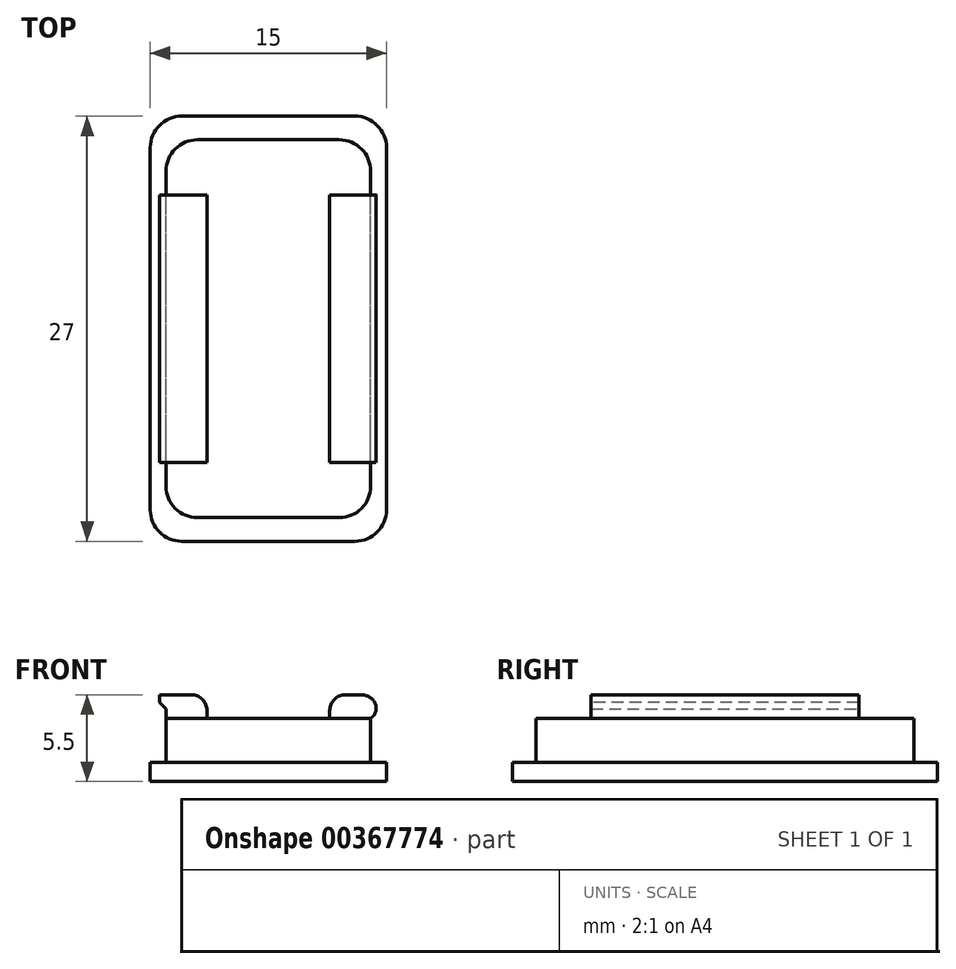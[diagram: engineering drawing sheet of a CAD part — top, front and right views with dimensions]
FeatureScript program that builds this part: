
annotation { "Feature Type Name" : "Feature", "Feature Type Description" : "" }
export const myFeature = defineFeature(function(context is Context, id is Id, definition is map)
    precondition{}
    {
        {
            var Q0;
            Q0=qCreatedBy(makeId("Top.planeOp"),FACE);
            var sketch = newSketch(context, id + "F0", { "sketchPlane" : qUnion([Q0])});
            skLineSegment(sketch, "E0.bottom", {"start": v(6.5, -12) * mm, "end": v(-6.5, -12) * mm});
            skLineSegment(sketch, "E0.top", {"start": v(6.5, 12) * mm, "end": v(-6.5, 12) * mm});
            skLineSegment(sketch, "E0.left", {"start": v(6.5, -12) * mm, "end": v(6.5, 12) * mm});
            skLineSegment(sketch, "E0.right", {"start": v(-6.5, -12) * mm, "end": v(-6.5, 12) * mm});
            skPoint(sketch, "E0.middle", {"position": v(0, 0) * mm});
            skLineSegment(sketch, "E1.bottom", {"start": v(7.5, -13.5) * mm, "end": v(-7.5, -13.5) * mm});
            skLineSegment(sketch, "E1.top", {"start": v(7.5, 13.5) * mm, "end": v(-7.5, 13.5) * mm});
            skLineSegment(sketch, "E1.left", {"start": v(7.5, -13.5) * mm, "end": v(7.5, 13.5) * mm});
            skLineSegment(sketch, "E1.right", {"start": v(-7.5, -13.5) * mm, "end": v(-7.5, 13.5) * mm});
            skSolve(sketch);
        }
        {
            var Q0;
            Q0 = qSketchRegion(id + "F0", true);
            extrude(context, id + "F1", {"entities" : qUnion([Q0]), "depth" : 1.2 * mm});
        }
        {
            var Q0;
            Q0=makeQuery(id+"F0.imprint","IMPRINT",FACE,{"disambiguationData":[TD([[makeQuery(id+"F0.imprint","IMPRINT",EDGE,{"derivedFrom":sQuery(id+"F0.wireOp",EDGE,"E0.bottom")}),-1.0]])]});
            extrude(context, id + "F2", {"entities" : qUnion([Q0]), "operationType" : NewBodyOperationType.ADD, "depth" : 4 * mm});
        }
        {
            var Q0;
            Q0=makeQuery(id+"F2.opExtrude","SWEPT_EDGE",EDGE,{"disambiguationData":[OSD([sQuery(id+"F0.wireOp",EDGE,"E0.top"),sQuery(id+"F0.wireOp",EDGE,"E0.left")])]});
            var Q1;
            Q1=makeQuery(id+"F1.opExtrude","SWEPT_EDGE",EDGE,{"disambiguationData":[OSD([sQuery(id+"F0.wireOp",EDGE,"E1.top"),sQuery(id+"F0.wireOp",EDGE,"E1.left")])]});
            var Q2;
            Q2=makeQuery(id+"F2.opExtrude","SWEPT_EDGE",EDGE,{"disambiguationData":[OSD([sQuery(id+"F0.wireOp",EDGE,"E0.top"),sQuery(id+"F0.wireOp",EDGE,"E0.right")])]});
            var Q3;
            Q3=makeQuery(id+"F1.opExtrude","SWEPT_EDGE",EDGE,{"disambiguationData":[OSD([sQuery(id+"F0.wireOp",EDGE,"E1.top"),sQuery(id+"F0.wireOp",EDGE,"E1.right")])]});
            var Q4;
            Q4=makeQuery(id+"F2.opExtrude","SWEPT_EDGE",EDGE,{"disambiguationData":[OSD([sQuery(id+"F0.wireOp",EDGE,"E0.bottom"),sQuery(id+"F0.wireOp",EDGE,"E0.right")])]});
            var Q5;
            Q5=makeQuery(id+"F1.opExtrude","SWEPT_EDGE",EDGE,{"disambiguationData":[OSD([sQuery(id+"F0.wireOp",EDGE,"E1.bottom"),sQuery(id+"F0.wireOp",EDGE,"E1.right")])]});
            var Q6;
            Q6=makeQuery(id+"F1.opExtrude","SWEPT_EDGE",EDGE,{"disambiguationData":[OSD([sQuery(id+"F0.wireOp",EDGE,"E1.bottom"),sQuery(id+"F0.wireOp",EDGE,"E1.left")])]});
            var Q7;
            Q7=makeQuery(id+"F2.opExtrude","SWEPT_EDGE",EDGE,{"disambiguationData":[OSD([sQuery(id+"F0.wireOp",EDGE,"E0.bottom"),sQuery(id+"F0.wireOp",EDGE,"E0.left")])]});
            fillet(context, id + "F3", {"entities" : qUnion([Q0, Q1, Q2, Q3, Q4, Q5, Q6, Q7]), "radius" : 2 * mm, "tangentPropagation" : true, "allowEdgeOverflow" : false});
        }
        {
            var Q0;
            Q0=makeQuery(id+"F2.opExtrude","CAP_FACE",FACE,{"disambiguationData":[OSD([sQuery(id+"F0.wireOp",EDGE,"E0.bottom"),sQuery(id+"F0.wireOp",EDGE,"E0.top"),sQuery(id+"F0.wireOp",EDGE,"E0.left"),sQuery(id+"F0.wireOp",EDGE,"E0.right")])],"isStart":false});
            var sketch = newSketch(context, id + "F4", { "sketchPlane" : qUnion([Q0])});
            skLineSegment(sketch, "E2.bottom", {"start": v(6.9, -8.5) * mm, "end": v(-6.9, -8.5) * mm});
            skLineSegment(sketch, "E2.top", {"start": v(6.9, 8.5) * mm, "end": v(-6.9, 8.5) * mm});
            skLineSegment(sketch, "E2.left", {"start": v(6.9, -8.5) * mm, "end": v(6.9, 8.5) * mm});
            skLineSegment(sketch, "E2.right", {"start": v(-6.9, -8.5) * mm, "end": v(-6.9, 8.5) * mm});
            skPoint(sketch, "E2.middle", {"position": v(0, 0) * mm});
            skLineSegment(sketch, "E3", {"start": v(-3.9, 8.5) * mm, "end": v(-3.9, -8.5) * mm});
            skLineSegment(sketch, "E4.MirrorCS", {"start": v(3.9, 8.5) * mm, "end": v(3.9, -8.5) * mm});
            skSolve(sketch);
        }
        {
            var Q0;
            {var subQ0=sQuery(id+"F4.wireOp",EDGE,"E3");Q0=makeQuery(id+"F4.imprint","IMPRINT",FACE,{"disambiguationData":[TD([[makeQuery(id+"F4.imprint","IMPRINT",EDGE,{"derivedFrom":subQ0}),-1.0]])]});}
            var Q1;
            {var subQ0=sQuery(id+"F4.wireOp",EDGE,"E2.left");Q1=makeQuery(id+"F4.imprint","IMPRINT",FACE,{"disambiguationData":[TD([[makeQuery(id+"F4.imprint","IMPRINT",EDGE,{"derivedFrom":subQ0}),1.0]])]});}
            var Q2;
            {var subQ0=sQuery(id+"F4.wireOp",EDGE,"E4.MirrorCS");Q2=makeQuery(id+"F4.imprint","IMPRINT",FACE,{"disambiguationData":[TD([[makeQuery(id+"F4.imprint","IMPRINT",EDGE,{"derivedFrom":subQ0}),1.0]])]});}
            var Q3;
            {var subQ0=sQuery(id+"F4.wireOp",EDGE,"E2.right");Q3=makeQuery(id+"F4.imprint","IMPRINT",FACE,{"disambiguationData":[TD([[makeQuery(id+"F4.imprint","IMPRINT",EDGE,{"derivedFrom":subQ0}),-1.0]])]});}
            extrude(context, id + "F5", {"entities" : qUnion([Q0, Q1, Q2, Q3]), "operationType" : NewBodyOperationType.ADD, "depth" : 1.5 * mm});
        }
        {
            var Q0;
            Q0=makeQuery(id+"F5.opExtrude","CAP_EDGE",EDGE,{"disambiguationData":[OSD([sQuery(id+"F4.wireOp",EDGE,"E2.left")])],"isStart":true});
            var Q1;
            Q1=makeQuery(id+"F5.opExtrude","CAP_EDGE",EDGE,{"disambiguationData":[OSD([sQuery(id+"F4.wireOp",EDGE,"E2.left")])],"isStart":false});
            var Q2;
            Q2=makeQuery(id+"F5.opExtrude","CAP_EDGE",EDGE,{"disambiguationData":[OSD([sQuery(id+"F4.wireOp",EDGE,"E3")])],"isStart":false});
            var Q3;
            Q3=makeQuery(id+"F5.opExtrude","CAP_EDGE",EDGE,{"disambiguationData":[OSD([sQuery(id+"F4.wireOp",EDGE,"E4.MirrorCS")])],"isStart":false});
            fillet(context, id + "F6", {"entities" : qUnion([Q0, Q1, Q2, Q3]), "radius" : 1 * mm, "tangentPropagation" : true, "allowEdgeOverflow" : false});
        }
        {
            var Q0;
            Q0=makeQuery(id+"F5.opExtrude","CAP_EDGE",EDGE,{"disambiguationData":[OSD([sQuery(id+"F4.wireOp",EDGE,"E2.right")])],"isStart":true});
            chamfer(context, id + "F7", {"entities" : qUnion([Q0]), "width" : 1 * mm, "tangentPropagation" : true});
        }
        {
            var Q0;
            {var subQ0=sQuery(id+"F4.wireOp",EDGE,"E2.left");Q0=makeQuery(id+"F6.opFillet","BLEND_EDGE",EDGE,{"blendedFrom":[makeQuery(id+"F5.opExtrude","CAP_EDGE",EDGE,{"disambiguationData":[OSD([subQ0])],"isStart":true}),makeQuery(id+"F5.opExtrude","CAP_EDGE",EDGE,{"disambiguationData":[OSD([subQ0])],"isStart":false})],"blendedInto":[]});}
            fillet(context, id + "F8", {"entities" : qUnion([Q0]), "radius" : .75 * mm, "tangentPropagation" : true, "allowEdgeOverflow" : false});
        }
    });
